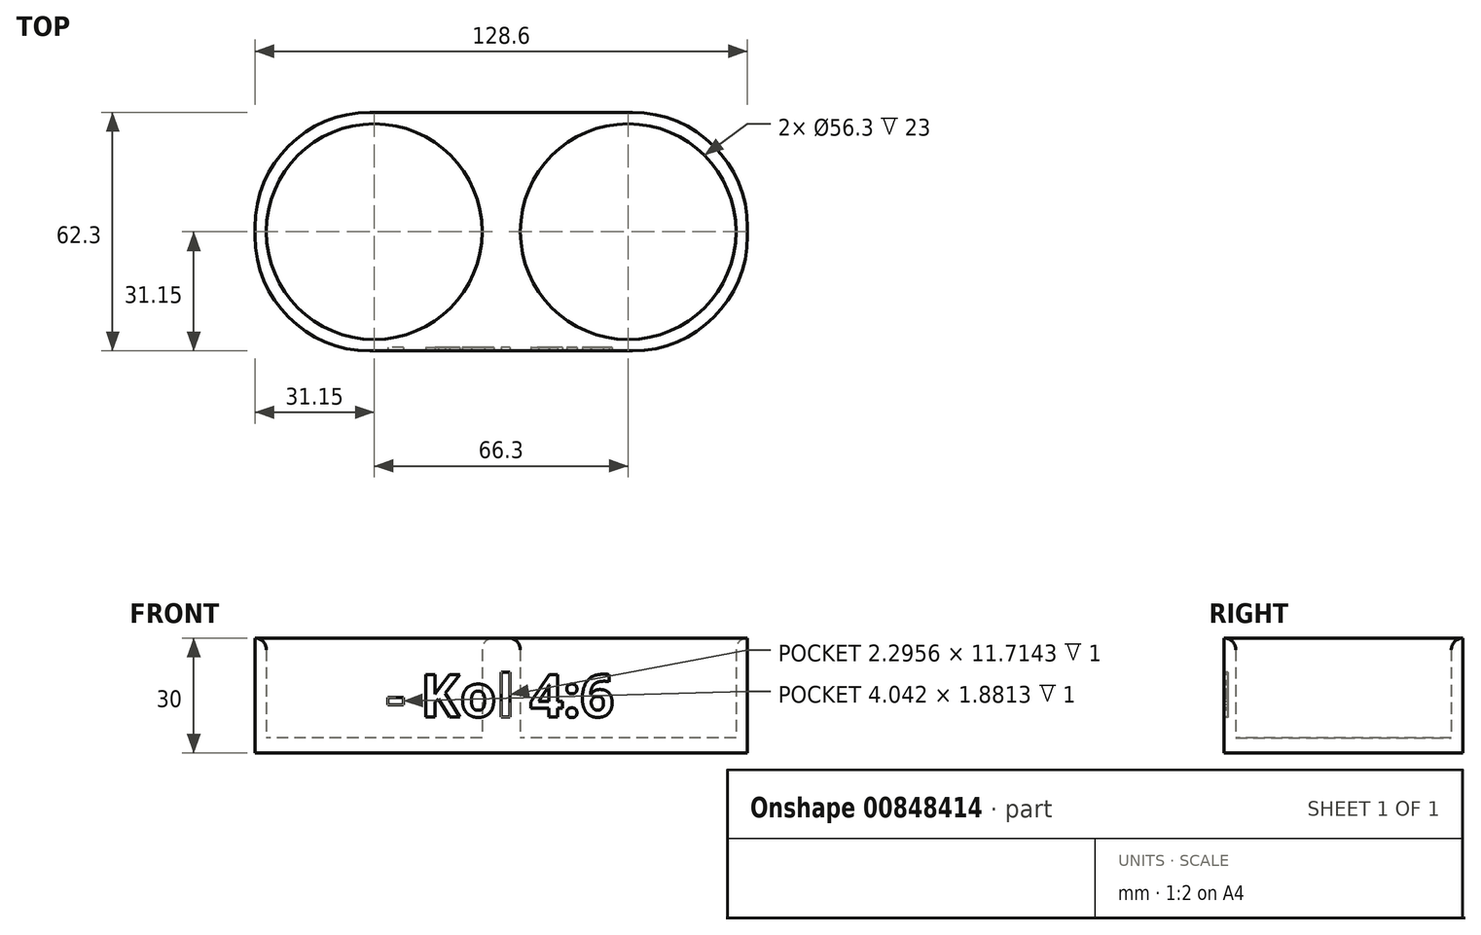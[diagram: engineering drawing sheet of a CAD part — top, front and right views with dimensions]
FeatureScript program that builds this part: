
annotation { "Feature Type Name" : "Feature", "Feature Type Description" : "" }
export const myFeature = defineFeature(function(context is Context, id is Id, definition is map)
    precondition{}
    {
        {
            var Q0;
            Q0=qCreatedBy(makeId("Top.planeOp"),FACE);
            var sketch = newSketch(context, id + "F0", { "sketchPlane" : qUnion([Q0])});
            skLineSegment(sketch, "E0.bottom", {"start": v(64.3, 31.15) * mm, "end": v(-64.3, 31.15) * mm});
            skLineSegment(sketch, "E0.top", {"start": v(64.3, -31.15) * mm, "end": v(-64.3, -31.15) * mm});
            skLineSegment(sketch, "E0.left", {"start": v(64.3, 31.15) * mm, "end": v(64.3, -31.15) * mm});
            skLineSegment(sketch, "E0.right", {"start": v(-64.3, 31.15) * mm, "end": v(-64.3, -31.15) * mm});
            skPoint(sketch, "E0.middle", {"position": v(0, 0) * mm});
            skCircle(sketch, "E1", {"center": v(-33.15, 0) * mm, "radius": 28.15 * mm});
            skCircle(sketch, "E2", {"center": v(33.15, 0) * mm, "radius": 28.15 * mm});
            skSolve(sketch);
        }
        {
            var Q0;
            Q0=makeQuery(id+"F0.imprint","IMPRINT",FACE,{"disambiguationData":[TD([[makeQuery(id+"F0.imprint","IMPRINT",EDGE,{"derivedFrom":sQuery(id+"F0.wireOp",EDGE,"E0.bottom")}),1.0]])]});
            extrude(context, id + "F1", {"entities" : qUnion([Q0]), "flatOperationType" : FlatOperationType.REMOVE, "depth" : 30 * mm, "offsetDistance" : 25 * mm, "domain" : OperationDomain.MODEL});
        }
        {
            var Q0;
            Q0=makeQuery(id+"F0.imprint","IMPRINT",FACE,{"disambiguationData":[TD([[makeQuery(id+"F0.imprint","IMPRINT",EDGE,{"derivedFrom":sQuery(id+"F0.wireOp",EDGE,"E1")}),1.0]])]});
            var Q1;
            Q1=makeQuery(id+"F0.imprint","IMPRINT",FACE,{"disambiguationData":[TD([[makeQuery(id+"F0.imprint","IMPRINT",EDGE,{"derivedFrom":sQuery(id+"F0.wireOp",EDGE,"E2")}),1.0]])]});
            extrude(context, id + "F2", {"entities" : qUnion([Q0, Q1]), "operationType" : NewBodyOperationType.ADD, "flatOperationType" : FlatOperationType.REMOVE, "depth" : 4 * mm, "offsetDistance" : 25 * mm, "domain" : OperationDomain.MODEL});
        }
        {
            var Q0;
            Q0=makeQuery(id+"F1.opExtrude","SWEPT_EDGE",EDGE,{"disambiguationData":[OSD([sQuery(id+"F0.wireOp",EDGE,"E0.bottom"),sQuery(id+"F0.wireOp",EDGE,"E0.right")])]});
            var Q1;
            Q1=makeQuery(id+"F1.opExtrude","SWEPT_EDGE",EDGE,{"disambiguationData":[OSD([sQuery(id+"F0.wireOp",EDGE,"E0.top"),sQuery(id+"F0.wireOp",EDGE,"E0.right")])]});
            var Q2;
            Q2=makeQuery(id+"F1.opExtrude","SWEPT_EDGE",EDGE,{"disambiguationData":[OSD([sQuery(id+"F0.wireOp",EDGE,"E0.top"),sQuery(id+"F0.wireOp",EDGE,"E0.left")])]});
            var Q3;
            Q3=makeQuery(id+"F1.opExtrude","SWEPT_EDGE",EDGE,{"disambiguationData":[OSD([sQuery(id+"F0.wireOp",EDGE,"E0.bottom"),sQuery(id+"F0.wireOp",EDGE,"E0.left")])]});
            fillet(context, id + "F3", {"entities" : qUnion([Q0, Q1, Q2, Q3]), "radius" : 30 * mm, "tangentPropagation" : true, "defaultsChanged" : false, "vertexSettings" : [], "allowEdgeOverflow" : false});
        }
        {
            var Q0;
            Q0=makeQuery(id+"F1.opExtrude","CAP_EDGE",EDGE,{"disambiguationData":[OSD([sQuery(id+"F0.wireOp",EDGE,"E1")])],"isStart":false});
            var Q1;
            Q1=makeQuery(id+"F1.opExtrude","CAP_EDGE",EDGE,{"disambiguationData":[OSD([sQuery(id+"F0.wireOp",EDGE,"E2")])],"isStart":false});
            fillet(context, id + "F4", {"entities" : qUnion([Q0, Q1]), "radius" : 3 * mm, "tangentPropagation" : true, "allowEdgeOverflow" : false});
        }
        {
            var Q0;
            Q0=makeQuery(id+"F1.opExtrude","SWEPT_FACE",FACE,{"disambiguationData":[OSD([sQuery(id+"F0.wireOp",EDGE,"E0.top")])]});
            var sketch = newSketch(context, id + "F5", { "sketchPlane" : qUnion([Q0])});
            skText(sketch, "E3", { "text": "- Kol 4:6", "fontName": "OpenSans-Bold.ttf"});
            const initialGuessF5  = {"E3": [-0.03, 0.00945, 1, 0, 0.0111]};
            skSetInitialGuess(sketch, initialGuessF5);
            skSolve(sketch);
        }
        {
            var Q0;
            Q0 = qSketchRegion(id + "F5", true);
            extrude(context, id + "F6", {"entities" : qUnion([Q0]), "operationType" : NewBodyOperationType.REMOVE, "oppositeDirection" : true, "depth" : 1 * mm, "offsetDistance" : 25 * mm});
        }
    });
